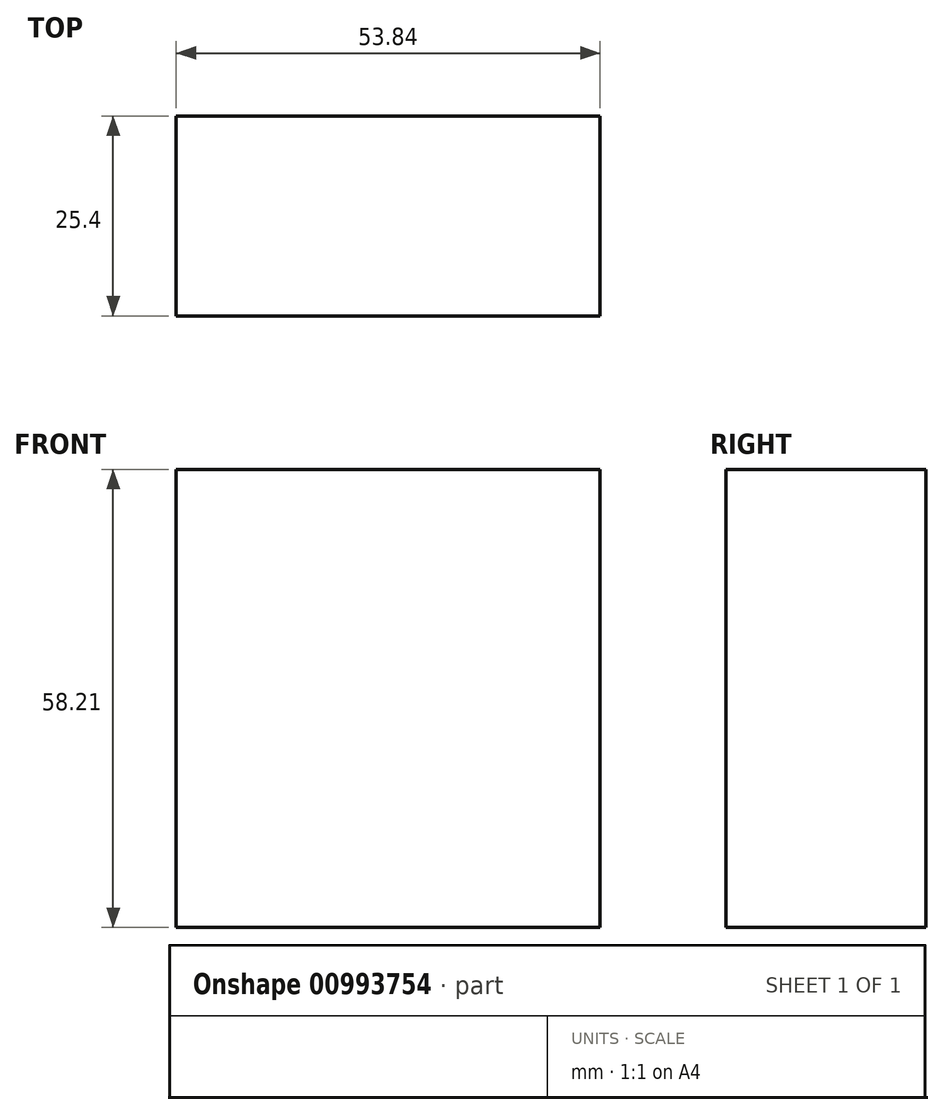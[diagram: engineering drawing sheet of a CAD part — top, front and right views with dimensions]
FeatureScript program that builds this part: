
annotation { "Feature Type Name" : "Feature", "Feature Type Description" : "" }
export const myFeature = defineFeature(function(context is Context, id is Id, definition is map)
    precondition{}
    {
        {
            var Q0;
            Q0=qCreatedBy(makeId("Front.planeOp"),FACE);
            var sketch = newSketch(context, id + "F0", { "sketchPlane" : qUnion([Q0])});
            skLineSegment(sketch, "E0.bottom", {"start": v(-14.12, 27.4) * mm, "end": v(39.72, 27.4) * mm});
            skLineSegment(sketch, "E0.top", {"start": v(-14.12, -30.8) * mm, "end": v(39.72, -30.8) * mm});
            skLineSegment(sketch, "E0.left", {"start": v(-14.12, 27.4) * mm, "end": v(-14.12, -30.8) * mm});
            skLineSegment(sketch, "E0.right", {"start": v(39.72, 27.4) * mm, "end": v(39.72, -30.8) * mm});
            skSolve(sketch);
        }
        {
            var Q0;
            Q0=makeQuery(id+"F0.imprint","IMPRINT",FACE,{"disambiguationData":[TD([[makeQuery(id+"F0.imprint","IMPRINT",EDGE,{"derivedFrom":sQuery(id+"F0.wireOp",EDGE,"E0.bottom")}),-1.0]])]});
            extrude(context, id + "F1", {"entities" : qUnion([Q0]), "depth" : 25.4 * mm, "offsetDistance" : 25.4 * mm});
        }
    });
